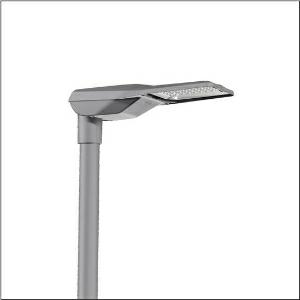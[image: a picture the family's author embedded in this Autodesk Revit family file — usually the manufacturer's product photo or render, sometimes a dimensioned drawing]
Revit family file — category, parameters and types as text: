
# Revit family: streetlight_sl_21_iq_mini___st1_0ab_5xe2m31g08jb_9670
name_source: partatom
category: Lighting Fixtures
units: mm (PartAtom-declared; Revit-internal decimal feet)

## family parameters
Cut with Voids When Loaded = No
Host = Face
Light Source = No
Part Type = Normal
Room Calculation Point = No
Round Connector Dimension = Use Diameter
Shared = No

## types (1)
- --- (1 x LED, 9530 lm, 71.6 W, 3000K)
    Apparent Load = 72 VA
    CIE Flux Codes = 40 74 97 100 100
    Color Rendering = 70
    Color Temperature = 3000K
    Default Elevation = 1800 mm
    Description = Streetlight SL 21 iQ mini, mast luminaire, primary light control with lens, of PMMA, primary optical cover: cover, of toughened safety glass, transparent, light distribution: ST1.0aB, light emission: direct distribution, primary light characteristic: asymmetric, installation type: post-top, side-entry, LED, High Power LED, rated luminous flux: 9.530lm, luminous efficacy: 133lm/W, light colour: 730, colour temperature: 3000K, control gear: iQ Street-Remote, control: Street-Remote, Auto-Match, Temp-Guard, Lumen-Switch, Night-Set, Smart-Wire, Light-Fading, Desk-Remote (wireless, voltage-free reading and setting of iQ features in the workshop via application-optimized NFC function/RFID function), optimised constant luminous flux control (CLO 2.0), pre-setting: linear dimming characteristic, mains connection: 220..240V, AC, 50/60Hz, start of lifetime: 72W, end of service life: 75W, reduction: 33W, luminaire housing, of diecast aluminium, powder-coated, SITECO metallic grey (DB 702S), corrosivity category C5 high according to DIN EN ISO 12944, please order mast flange separately, inclination adjustable: 0°, 5°, 10°, 15°, sealing non-destructively replaceable, multi-level sealing system, length: 628mm, width: 235mm, height: 110mm, mast flange for spigot size: 42mm (side-entry): 5XC10008XM4, 60/48mm (side-entry/post-top): 5XC10108XM2, 76/60mm (side-entry/post-top): 5XC10108XM1, mounting height: 4..8m, protection rating (complete): IP66, insulation class (complete): insulation class II (safety insulation), certification: CE, ENEC, ENEC+, VDE, impact resistance: IK10, permissible operating ambient temperature for outdoor applications: -40..+50°C, standard-compliant lighting for roads and squares, packaging unit: 1 piece

Light Distribution: ST1.0aB
    Height = 110 mm
    Lamp = 1 x LED
    Lamp Light Flux = 9530 lm
    Lamp Power = 71.6 W
    Lamp count = 1
    Length = 625 mm
    Luminous efficacy = 133 lm/W
    Manufacturer = Siteco
    ModVariant = No
    Model = 5XE2M31G08JB
    Number of Poles = 1
    OnlyDefault = Yes
    Power Factor = 1
    Product Name = Streetlight SL 21 iQ mini | ST1.0aB
    Product group = mast luminaire | pylon top
    ProductGroupID = 6100
    Protection Class = Protection class II
    Protection Degree = IP 66
    RLX_Detail_Level = 1
    RLX_Emergency_Light_Flux = 0 lm
    RLX_Emergency_Type = 0
    RLX_Emergency_Type_DB = No
    RlxData = <blob elided: 26341 chars, md5=83306475>
    Socket = socket
    Standby Power = 0 W
    System Light Flux = 9530 lm
    System Power = 72 W
    Type Comments = factory setting: luminous flux: 100 % | dim-lin: 254 | 746 mA
    Type Image = l_1003519.jpg
    URL = http://relux.com
    VarID = @adj_167817
    Voltage = 0 V
    Weight = 0.00 kg
    Width = 234 mm

## geometry (parser evidence)
native form markers: Blend x4, Sweep x13
no freeform markers — native parametric forms only
